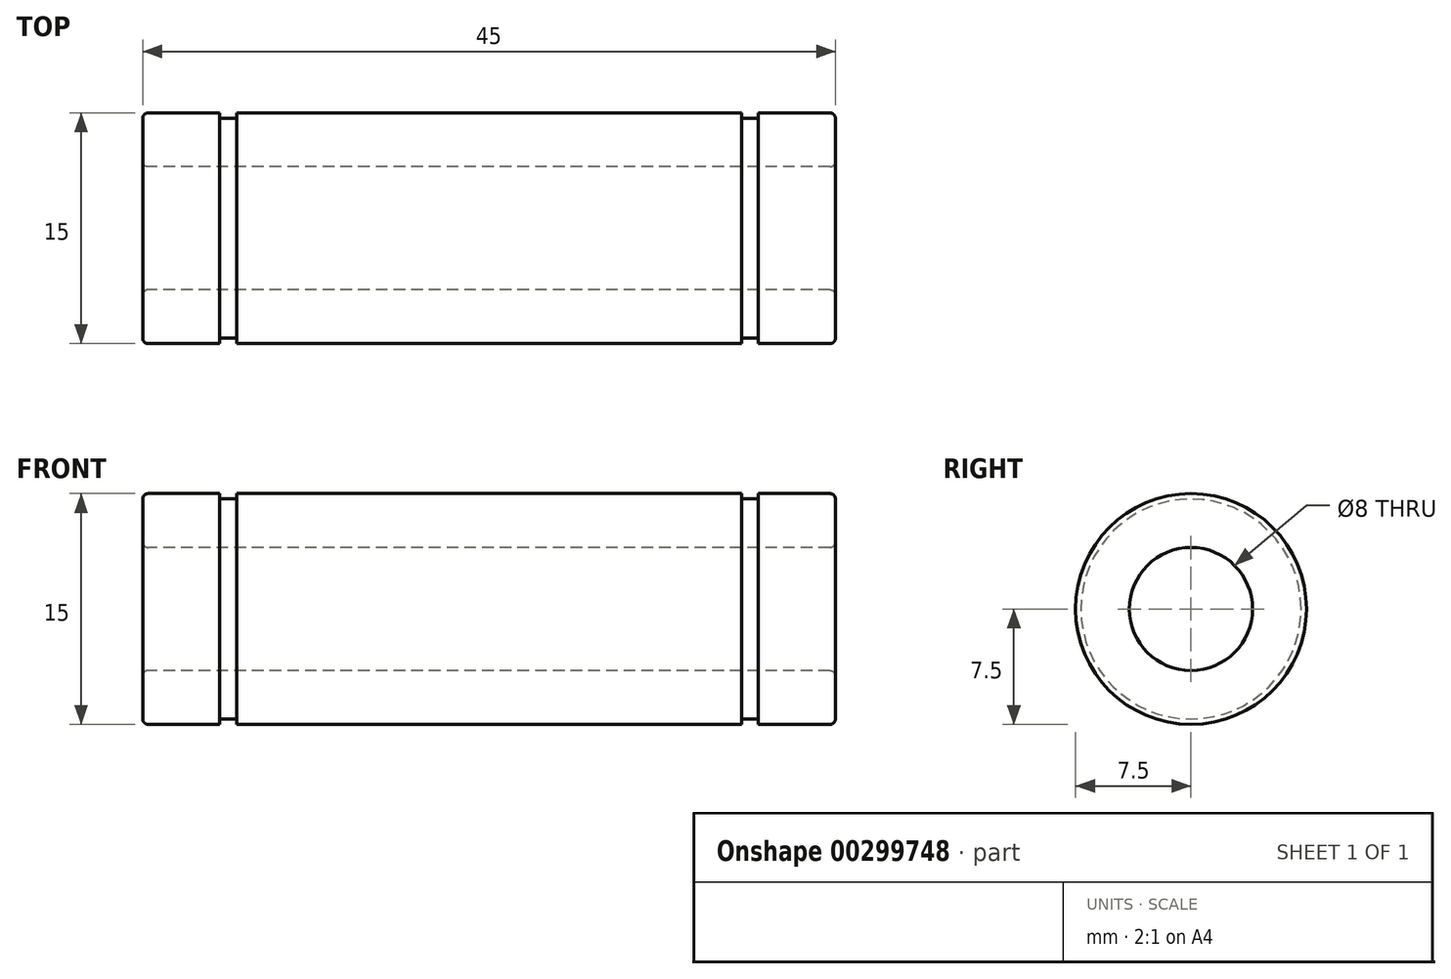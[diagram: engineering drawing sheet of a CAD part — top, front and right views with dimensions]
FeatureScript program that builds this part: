
annotation { "Feature Type Name" : "Feature", "Feature Type Description" : "" }
export const myFeature = defineFeature(function(context is Context, id is Id, definition is map)
    precondition{}
    {
        {
            var Q0;
            Q0=qCreatedBy(makeId("Top.planeOp"),FACE);
            var sketch = newSketch(context, id + "F0", { "sketchPlane" : qUnion([Q0])});
            skLineSegment(sketch, "E0.bottom", {"start": v(-22.15, 7.5) * mm, "end": v(-17.5, 7.5) * mm});
            skLineSegment(sketch, "E0.top", {"start": v(-22.15, -7.5) * mm, "end": v(-17.5, -7.5) * mm});
            skLineSegment(sketch, "E0.left", {"start": v(-22.5, 7.15) * mm, "end": v(-22.5, -7.15) * mm});
            skLineSegment(sketch, "E0.right", {"start": v(22.5, 7.15) * mm, "end": v(22.5, -7.15) * mm});
            skPoint(sketch, "E0.middle", {"position": v(0, 0) * mm});
            skLineSegment(sketch, "E1", {"start": v(-17.5, 7.5) * mm, "end": v(-17.5, 7.15) * mm});
            skLineSegment(sketch, "E2", {"start": v(-16.4, 7.5) * mm, "end": v(-16.4, 7.15) * mm});
            skLineSegment(sketch, "E3", {"start": v(16.4, 7.5) * mm, "end": v(16.4, 7.15) * mm});
            skLineSegment(sketch, "E4", {"start": v(17.5, 7.5) * mm, "end": v(17.5, 7.15) * mm});
            skArc(sketch, "E5.filletArc", {"start": v(22.5, 7.15) * mm, "mid": v(22.4, 7.4) * mm, "end": v(22.15, 7.5) * mm});
            skArc(sketch, "E6.filletArc", {"start": v(22.15, -7.5) * mm, "mid": v(22.4, -7.4) * mm, "end": v(22.5, -7.15) * mm});
            skArc(sketch, "E7.filletArc", {"start": v(-22.15, 7.5) * mm, "mid": v(-22.4, 7.4) * mm, "end": v(-22.5, 7.15) * mm});
            skArc(sketch, "E8.filletArc", {"start": v(-22.5, -7.15) * mm, "mid": v(-22.4, -7.4) * mm, "end": v(-22.15, -7.5) * mm});
            skLineSegment(sketch, "E9.trimOffspring", {"start": v(-16.4, 7.5) * mm, "end": v(16.4, 7.5) * mm});
            skLineSegment(sketch, "E10.trimOffspring", {"start": v(-16.4, -7.5) * mm, "end": v(16.4, -7.5) * mm});
            skLineSegment(sketch, "E11.trimOffspring", {"start": v(17.5, 7.5) * mm, "end": v(22.15, 7.5) * mm});
            skLineSegment(sketch, "E12.trimOffspring", {"start": v(17.5, -7.5) * mm, "end": v(22.15, -7.5) * mm});
            skLineSegment(sketch, "E13", {"start": v(-17.5, 7.15) * mm, "end": v(-16.4, 7.15) * mm});
            skLineSegment(sketch, "E14", {"start": v(-17.5, -7.15) * mm, "end": v(-16.4, -7.15) * mm});
            skLineSegment(sketch, "E15", {"start": v(16.4, 7.15) * mm, "end": v(17.5, 7.15) * mm});
            skLineSegment(sketch, "E16", {"start": v(16.4, -7.15) * mm, "end": v(17.5, -7.15) * mm});
            skLineSegment(sketch, "E17", {"start": v(-22.5, 0) * mm, "end": v(22.5, 0) * mm, "construction": true});
            skLineSegment(sketch, "E18", {"start": v(-22.15, 4) * mm, "end": v(22.15, 4) * mm});
            skLineSegment(sketch, "E19", {"start": v(-22.15, -4) * mm, "end": v(22.5, -4) * mm});
            skArc(sketch, "E20", {"start": v(-22.5, 4.35) * mm, "mid": v(-22.4, 4.1) * mm, "end": v(-22.15, 4) * mm});
            skArc(sketch, "E21", {"start": v(-22.15, -4) * mm, "mid": v(-22.4, -4.1) * mm, "end": v(-22.5, -4.35) * mm});
            skArc(sketch, "E22", {"start": v(22.15, 4) * mm, "mid": v(22.4, 4.1) * mm, "end": v(22.5, 4.35) * mm});
            skArc(sketch, "E23", {"start": v(22.5, -4.35) * mm, "mid": v(22.4, -4.1) * mm, "end": v(22.15, -4) * mm});
            skPoint(sketch, "E24.orphan", {"position": v(-22.5, -4) * mm});
            skPoint(sketch, "E25.orphan", {"position": v(22.5, 4) * mm});
            skLineSegment(sketch, "E26.trimOffspring", {"start": v(17.5, -7.15) * mm, "end": v(17.5, -7.5) * mm});
            skLineSegment(sketch, "E27.trimOffspring", {"start": v(16.4, -7.15) * mm, "end": v(16.4, -7.5) * mm});
            skLineSegment(sketch, "E28.trimOffspring", {"start": v(-17.5, -7.15) * mm, "end": v(-17.5, -7.5) * mm});
            skLineSegment(sketch, "E29.trimOffspring", {"start": v(-16.4, -7.15) * mm, "end": v(-16.4, -7.5) * mm});
            skLineSegment(sketch, "E30", {"start": v(-17.5, 7.15) * mm, "end": v(-17.5, -7.15) * mm, "construction": true});
            skLineSegment(sketch, "E31", {"start": v(-16.4, -7.15) * mm, "end": v(-16.4, 7.15) * mm, "construction": true});
            skLineSegment(sketch, "E32", {"start": v(16.4, -7.15) * mm, "end": v(16.4, 7.15) * mm, "construction": true});
            skLineSegment(sketch, "E33", {"start": v(17.5, 7.15) * mm, "end": v(17.5, -7.15) * mm, "construction": true});
            skSolve(sketch);
        }
        {
            var Q0;
            {var subQ1=sQuery(id+"F0.wireOp",EDGE,"E0.bottom");Q0=makeQuery(id+"F0.imprint","IMPRINT",FACE,{"disambiguationData":[TD([[makeQuery(id+"F0.imprint","IMPRINT",EDGE,{"derivedFrom":subQ1}),-1.0]])]});}
            var Q1;
            {var subQ0=sQuery(id+"F0.wireOp",EDGE,"E13");Q1=makeQuery(id+"F0.imprint","IMPRINT",FACE,{"disambiguationData":[TD([[makeQuery(id+"F0.imprint","IMPRINT",EDGE,{"derivedFrom":subQ0}),-1.0]])]});}
            var Q2;
            {var subQ0=sQuery(id+"F0.wireOp",EDGE,"E9.trimOffspring");Q2=makeQuery(id+"F0.imprint","IMPRINT",FACE,{"disambiguationData":[TD([[makeQuery(id+"F0.imprint","IMPRINT",EDGE,{"derivedFrom":subQ0}),-1.0]])]});}
            var Q3;
            {var subQ0=sQuery(id+"F0.wireOp",EDGE,"E15");Q3=makeQuery(id+"F0.imprint","IMPRINT",FACE,{"disambiguationData":[TD([[makeQuery(id+"F0.imprint","IMPRINT",EDGE,{"derivedFrom":subQ0}),-1.0]])]});}
            var Q4;
            {var subQ0=sQuery(id+"F0.wireOp",EDGE,"E5.filletArc");Q4=makeQuery(id+"F0.imprint","IMPRINT",FACE,{"disambiguationData":[TD([[makeQuery(id+"F0.imprint","IMPRINT",EDGE,{"derivedFrom":subQ0}),1.0]])]});}
            var Q5;
            Q5=sQuery(id+"F0.wireOp",EDGE,"E17");
            revolve(context, id + "F1", {"entities" : qUnion([Q0, Q1, Q2, Q3, Q4]), "axis" : qUnion([Q5]), "revolveType" : RevolveType.FULL});
        }
    });
